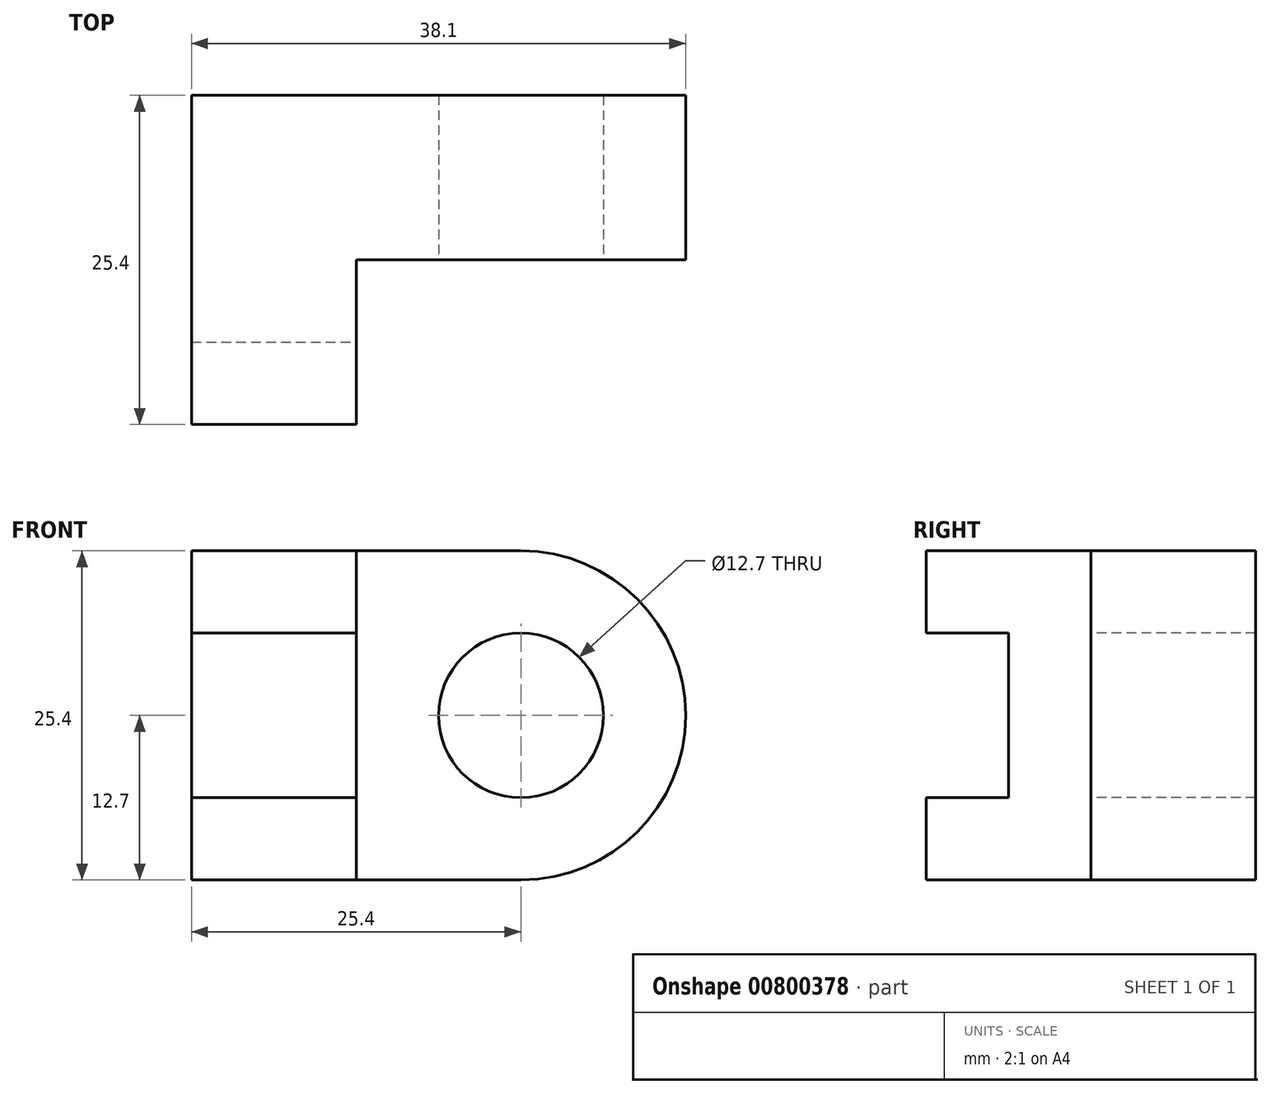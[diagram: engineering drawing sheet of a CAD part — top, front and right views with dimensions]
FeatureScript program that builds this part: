
annotation { "Feature Type Name" : "Feature", "Feature Type Description" : "" }
export const myFeature = defineFeature(function(context is Context, id is Id, definition is map)
    precondition{}
    {
        {
            var Q0;
            Q0=qCreatedBy(makeId("Right.planeOp"),FACE);
            var sketch = newSketch(context, id + "F0", { "sketchPlane" : qUnion([Q0])});
            skLineSegment(sketch, "E0", {"start": v(0, 0) * mm, "end": v(0, -25.4) * mm});
            skLineSegment(sketch, "E1", {"start": v(0, -25.4) * mm, "end": v(12.7, -25.4) * mm});
            skLineSegment(sketch, "E2", {"start": v(12.7, -25.4) * mm, "end": v(12.7, 0) * mm});
            skLineSegment(sketch, "E3", {"start": v(12.7, 0) * mm, "end": v(0, 0) * mm});
            skSolve(sketch);
        }
        {
            var Q0;
            Q0 = qSketchRegion(id + "F0", true);
            extrude(context, id + "F1", {"entities" : qUnion([Q0]), "depth" : 19.05 * mm, "offsetDistance" : 25.4 * mm});
        }
        {
            var Q0;
            Q0=makeQuery(id+"F1.opExtrude","SWEPT_FACE",FACE,{"disambiguationData":[OSD([sQuery(id+"F0.wireOp",EDGE,"E3")])]});
            var sketch = newSketch(context, id + "F2", { "sketchPlane" : qUnion([Q0])});
            skLineSegment(sketch, "E4", {"start": v(0, 0) * mm, "end": v(0, -12.7) * mm});
            skLineSegment(sketch, "E5", {"start": v(0, -12.7) * mm, "end": v(12.7, -12.7) * mm});
            skLineSegment(sketch, "E6", {"start": v(12.7, -12.7) * mm, "end": v(12.7, 0) * mm});
            skLineSegment(sketch, "E7", {"start": v(12.7, 0) * mm, "end": v(0, 0) * mm});
            skSolve(sketch);
        }
        {
            var Q0;
            Q0 = qSketchRegion(id + "F2", true);
            extrude(context, id + "F3", {"entities" : qUnion([Q0]), "operationType" : NewBodyOperationType.ADD, "oppositeDirection" : true, "depth" : 25.4 * mm, "offsetDistance" : 25.4 * mm});
        }
        {
            var Q0;
            Q0=makeQuery(id+"F3.opExtrude","SWEPT_FACE",FACE,{"disambiguationData":[OSD([sQuery(id+"F2.wireOp",EDGE,"E6")])]});
            var sketch = newSketch(context, id + "F4", { "sketchPlane" : qUnion([Q0])});
            skLineSegment(sketch, "E8", {"start": v(-12.7, -6.35) * mm, "end": v(-6.35, -6.35) * mm});
            skLineSegment(sketch, "E9", {"start": v(-6.35, -6.35) * mm, "end": v(-6.35, -19.05) * mm});
            skLineSegment(sketch, "E10", {"start": v(-6.35, -19.05) * mm, "end": v(-12.7, -19.05) * mm});
            skLineSegment(sketch, "E11", {"start": v(-12.7, -6.35) * mm, "end": v(-12.7, -19.05) * mm});
            skSolve(sketch);
        }
        {
            var Q0;
            Q0 = qSketchRegion(id + "F4", true);
            extrude(context, id + "F5", {"entities" : qUnion([Q0]), "operationType" : NewBodyOperationType.REMOVE, "oppositeDirection" : true, "depth" : 25.4 * mm, "offsetDistance" : 25.4 * mm});
        }
        {
            var Q0;
            Q0=makeQuery(id+"F1.opExtrude","SWEPT_FACE",FACE,{"disambiguationData":[OSD([sQuery(id+"F0.wireOp",EDGE,"E0")])]});
            var sketch = newSketch(context, id + "F6", { "sketchPlane" : qUnion([Q0])});
            skLineSegment(sketch, "E12", {"start": v(19.05, 0) * mm, "end": v(25.4, 0) * mm});
            skLineSegment(sketch, "E13", {"start": v(25.4, 0) * mm, "end": v(25.4, -25.4) * mm});
            skLineSegment(sketch, "E14", {"start": v(25.4, -25.4) * mm, "end": v(19.05, -25.4) * mm});
            skSolve(sketch);
        }
        {
            var Q0;
            Q0 = qSketchRegion(id + "F6", true);
            var Q1;
            Q1=makeQuery(id+"F6.imprint","IMPRINT",FACE,{"disambiguationData":[TD([[makeQuery(id+"F6.imprint","IMPRINT",EDGE,{"derivedFrom":sQuery(id+"F6.wireOp",EDGE,"E12")}),-1.0]])]});
            extrude(context, id + "F7", {"entities" : qUnion([Q0, Q1]), "operationType" : NewBodyOperationType.ADD, "oppositeDirection" : true, "depth" : 12.7 * mm, "offsetDistance" : 25.4 * mm});
        }
        {
            var Q0;
            {var subQ0=sQuery(id+"F0.wireOp",EDGE,"E0");Q0=makeQuery(id+"F7.boolean.opBoolean","MERGE",FACE,{"derivedFrom":[makeQuery(id+"F1.opExtrude","SWEPT_FACE",FACE,{"disambiguationData":[OSD([subQ0])]}),makeQuery(id+"F7.opExtrude","CAP_FACE",FACE,{"disambiguationData":[OSD([subQ0,sQuery(id+"F6.wireOp",EDGE,"E12"),sQuery(id+"F6.wireOp",EDGE,"E13"),sQuery(id+"F6.wireOp",EDGE,"E14")])],"isStart":true})]});}
            var sketch = newSketch(context, id + "F8", { "sketchPlane" : qUnion([Q0])});
            skLineSegment(sketch, "E15", {"start": v(25.4, -12.7) * mm, "end": v(25.4, 0) * mm, "construction": true});
            skLineSegment(sketch, "E16", {"start": v(25.4, -12.7) * mm, "end": v(25.4, -25.4) * mm, "construction": true});
            skArc(sketch, "E17", {"start": v(25.4, -25.4) * mm, "mid": v(38.1, -12.7) * mm, "end": v(25.4, 0) * mm});
            skSolve(sketch);
        }
        {
            var Q0;
            Q0 = qSketchRegion(id + "F8", true);
            var Q1;
            Q1=makeQuery(id+"F8.imprint","IMPRINT",FACE,{"disambiguationData":[TD([[makeQuery(id+"F8.imprint","IMPRINT",EDGE,{"derivedFrom":sQuery(id+"F8.wireOp",EDGE,"E17")}),1.0]])]});
            extrude(context, id + "F9", {"entities" : qUnion([Q0, Q1]), "operationType" : NewBodyOperationType.ADD, "oppositeDirection" : true, "depth" : 12.7 * mm, "offsetDistance" : 25.4 * mm});
        }
        {
            var Q0;
            {var subQ0=sQuery(id+"F6.wireOp",EDGE,"E13");var subQ1=sQuery(id+"F0.wireOp",EDGE,"E0");Q0=makeQuery(id+"F9.boolean.opBoolean","MERGE",FACE,{"derivedFrom":[makeQuery(id+"F7.boolean.opBoolean","MERGE",FACE,{"derivedFrom":[makeQuery(id+"F1.opExtrude","SWEPT_FACE",FACE,{"disambiguationData":[OSD([subQ1])]}),makeQuery(id+"F7.opExtrude","CAP_FACE",FACE,{"disambiguationData":[OSD([subQ1,sQuery(id+"F6.wireOp",EDGE,"E12"),subQ0,sQuery(id+"F6.wireOp",EDGE,"E14")])],"isStart":true})]}),makeQuery(id+"F9.opExtrude","CAP_FACE",FACE,{"disambiguationData":[OSD([subQ0,sQuery(id+"F8.wireOp",EDGE,"E17")])],"isStart":true})]});}
            var sketch = newSketch(context, id + "F10", { "sketchPlane" : qUnion([Q0])});
            skLineSegment(sketch, "E18", {"start": v(12.7, -12.7) * mm, "end": v(25.4, -12.7) * mm, "construction": true});
            skCircle(sketch, "E19", {"center": v(25.4, -12.7) * mm, "radius": 6.35 * mm});
            skSolve(sketch);
        }
        {
            var Q0;
            Q0 = qSketchRegion(id + "F10", true);
            extrude(context, id + "F11", {"entities" : qUnion([Q0]), "operationType" : NewBodyOperationType.REMOVE, "endBound" : BoundingType.THROUGH_ALL, "oppositeDirection" : true, "depth" : 25.4 * mm, "offsetDistance" : 25.4 * mm});
        }
    });
